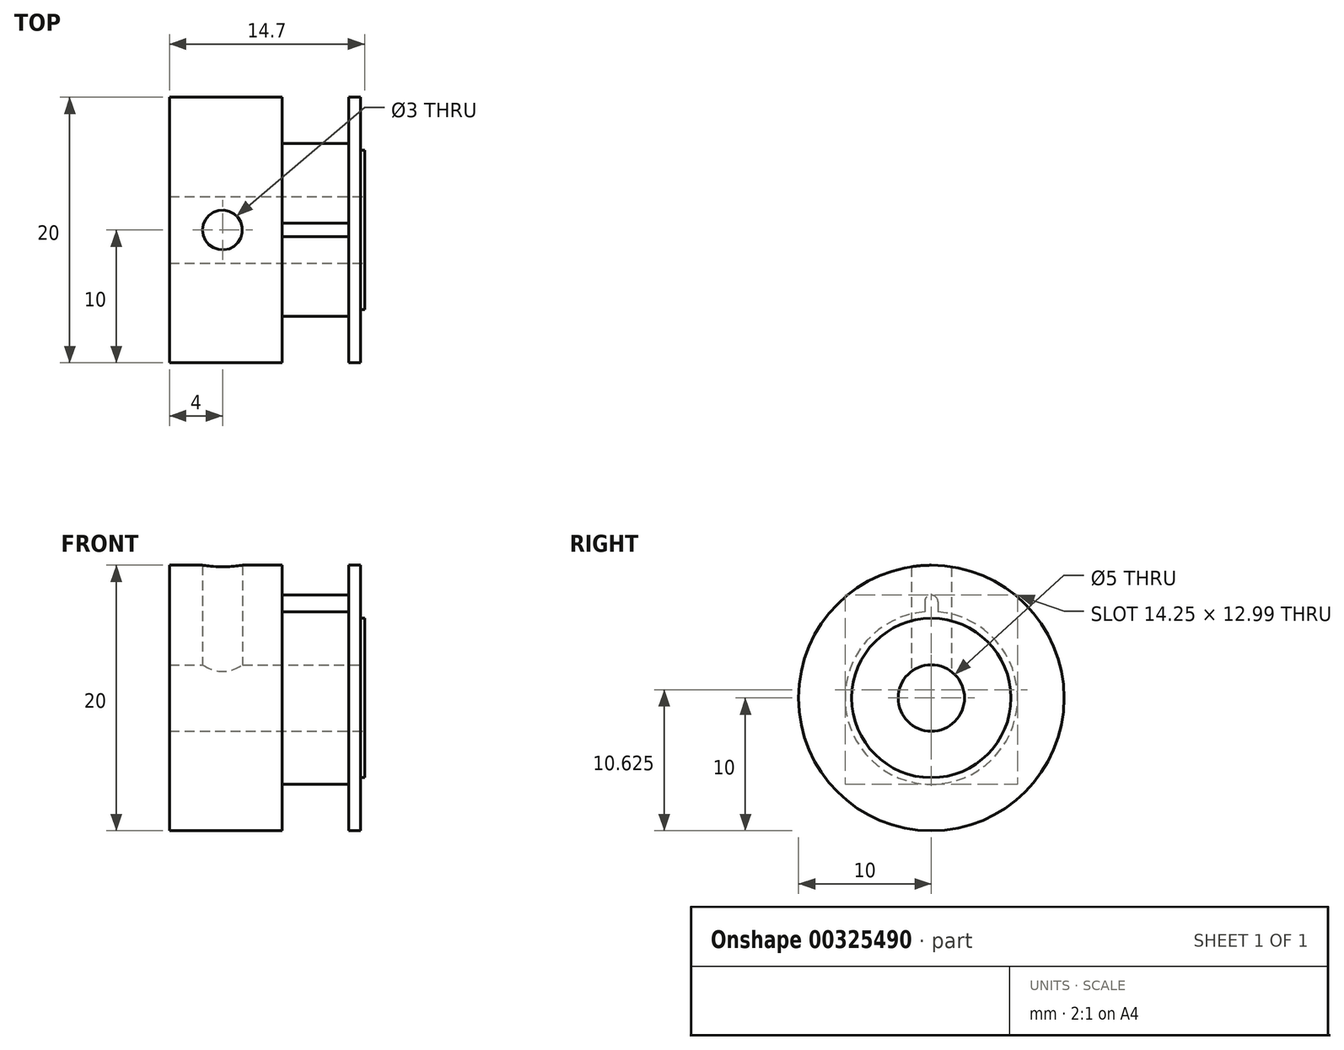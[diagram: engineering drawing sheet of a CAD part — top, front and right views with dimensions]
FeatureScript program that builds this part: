
annotation { "Feature Type Name" : "Feature", "Feature Type Description" : "" }
export const myFeature = defineFeature(function(context is Context, id is Id, definition is map)
    precondition{}
    {
        {
            var Q0;
            Q0=qCreatedBy(makeId("Right.planeOp"),FACE);
            var sketch = newSketch(context, id + "F0", { "sketchPlane" : qUnion([Q0])});
            skCircle(sketch, "E0", {"center": v(0, 0) * mm, "radius": 10 * mm});
            skSolve(sketch);
        }
        {
            var Q0;
            Q0 = qSketchRegion(id + "F0", true);
            extrude(context, id + "F1", {"entities" : qUnion([Q0]), "depth" : 8.5 * mm});
        }
        {
            var Q0;
            Q0=makeQuery(id+"F1.opExtrude","CAP_FACE",FACE,{"disambiguationData":[OSD([sQuery(id+"F0.wireOp",EDGE,"E0")])],"isStart":false});
            var sketch = newSketch(context, id + "F2", { "sketchPlane" : qUnion([Q0])});
            skLineSegment(sketch, "E1", {"start": v(0, 0) * mm, "end": v(0, 7.25) * mm, "construction": true});
            skArc(sketch, "E2", {"start": v(0.5, 7.25) * mm, "mid": v(0, 7.75) * mm, "end": v(-0.5, 7.25) * mm});
            skLineSegment(sketch, "E3", {"start": v(10, 0) * mm, "end": v(-10, 0) * mm, "construction": true});
            skArc(sketch, "E4", {"start": v(-0.5, 6.48) * mm, "mid": v(0, -6.5) * mm, "end": v(0.5, 6.48) * mm});
            skLineSegment(sketch, "E5", {"start": v(0.5, 7.25) * mm, "end": v(0.5, 6.48) * mm});
            skLineSegment(sketch, "E6", {"start": v(-0.5, 7.25) * mm, "end": v(-0.5, 6.48) * mm});
            skSolve(sketch);
        }
        {
            var Q0;
            Q0 = qSketchRegion(id + "F2", true);
            extrude(context, id + "F3", {"entities" : qUnion([Q0]), "operationType" : NewBodyOperationType.ADD, "depth" : 5 * mm});
        }
        {
            var Q0;
            Q0=qCreatedBy(makeId("Top.planeOp"),FACE);
            var sketch = newSketch(context, id + "F4", { "sketchPlane" : qUnion([Q0])});
            skLineSegment(sketch, "E7", {"start": v(0, 0) * mm, "end": v(13.5, 0) * mm, "construction": true});
            skSolve(sketch);
        }
        {
            var Q0;
            {var subQ0=sQuery(id+"F2.wireOp",EDGE,"E6");var subQ1=sQuery(id+"F2.wireOp",EDGE,"E5");var subQ2=sQuery(id+"F2.wireOp",EDGE,"E4");var subQ3=sQuery(id+"F2.wireOp",EDGE,"E2");Q0=makeQuery(id+"FyRSQMwNCxiUzVp_1.19.F3.boolean.opBoolean","MERGE",FACE,{"derivedFrom":[makeQuery(id+"FyRSQMwNCxiUzVp_1.18.F3.boolean.opBoolean","MERGE",FACE,{"derivedFrom":[makeQuery(id+"FyRSQMwNCxiUzVp_1.17.F3.boolean.opBoolean","MERGE",FACE,{"derivedFrom":[makeQuery(id+"FyRSQMwNCxiUzVp_1.16.F3.boolean.opBoolean","MERGE",FACE,{"derivedFrom":[makeQuery(id+"FyRSQMwNCxiUzVp_1.15.F3.boolean.opBoolean","MERGE",FACE,{"derivedFrom":[makeQuery(id+"FyRSQMwNCxiUzVp_1.14.F3.boolean.opBoolean","MERGE",FACE,{"derivedFrom":[makeQuery(id+"FyRSQMwNCxiUzVp_1.13.F3.boolean.opBoolean","MERGE",FACE,{"derivedFrom":[makeQuery(id+"FyRSQMwNCxiUzVp_1.12.F3.boolean.opBoolean","MERGE",FACE,{"derivedFrom":[makeQuery(id+"FyRSQMwNCxiUzVp_1.11.F3.boolean.opBoolean","MERGE",FACE,{"derivedFrom":[makeQuery(id+"FyRSQMwNCxiUzVp_1.10.F3.boolean.opBoolean","MERGE",FACE,{"derivedFrom":[makeQuery(id+"FyRSQMwNCxiUzVp_1.9.F3.boolean.opBoolean","MERGE",FACE,{"derivedFrom":[makeQuery(id+"FyRSQMwNCxiUzVp_1.8.F3.boolean.opBoolean","MERGE",FACE,{"derivedFrom":[makeQuery(id+"FyRSQMwNCxiUzVp_1.7.F3.boolean.opBoolean","MERGE",FACE,{"derivedFrom":[makeQuery(id+"FyRSQMwNCxiUzVp_1.6.F3.boolean.opBoolean","MERGE",FACE,{"derivedFrom":[makeQuery(id+"FyRSQMwNCxiUzVp_1.5.F3.boolean.opBoolean","MERGE",FACE,{"derivedFrom":[makeQuery(id+"FyRSQMwNCxiUzVp_1.4.F3.boolean.opBoolean","MERGE",FACE,{"derivedFrom":[makeQuery(id+"FyRSQMwNCxiUzVp_1.3.F3.boolean.opBoolean","MERGE",FACE,{"derivedFrom":[makeQuery(id+"FyRSQMwNCxiUzVp_1.2.F3.boolean.opBoolean","MERGE",FACE,{"derivedFrom":[makeQuery(id+"FyRSQMwNCxiUzVp_1.1.F3.boolean.opBoolean","MERGE",FACE,{"derivedFrom":[makeQuery(id+"F3.opExtrude","CAP_FACE",FACE,{"disambiguationData":[OSD([subQ3,subQ2,subQ1,subQ0])],"isStart":false}),makeQuery(id+"FyRSQMwNCxiUzVp_1.1.F3.opExtrude","CAP_FACE",FACE,{"disambiguationData":[OSD([subQ3,subQ2,subQ1,subQ0])],"isStart":false})]}),makeQuery(id+"FyRSQMwNCxiUzVp_1.2.F3.opExtrude","CAP_FACE",FACE,{"disambiguationData":[OSD([subQ3,subQ2,subQ1,subQ0])],"isStart":false})]}),makeQuery(id+"FyRSQMwNCxiUzVp_1.3.F3.opExtrude","CAP_FACE",FACE,{"disambiguationData":[OSD([subQ3,subQ2,subQ1,subQ0])],"isStart":false})]}),makeQuery(id+"FyRSQMwNCxiUzVp_1.4.F3.opExtrude","CAP_FACE",FACE,{"disambiguationData":[OSD([subQ3,subQ2,subQ1,subQ0])],"isStart":false})]}),makeQuery(id+"FyRSQMwNCxiUzVp_1.5.F3.opExtrude","CAP_FACE",FACE,{"disambiguationData":[OSD([subQ3,subQ2,subQ1,subQ0])],"isStart":false})]}),makeQuery(id+"FyRSQMwNCxiUzVp_1.6.F3.opExtrude","CAP_FACE",FACE,{"disambiguationData":[OSD([subQ3,subQ2,subQ1,subQ0])],"isStart":false})]}),makeQuery(id+"FyRSQMwNCxiUzVp_1.7.F3.opExtrude","CAP_FACE",FACE,{"disambiguationData":[OSD([subQ3,subQ2,subQ1,subQ0])],"isStart":false})]}),makeQuery(id+"FyRSQMwNCxiUzVp_1.8.F3.opExtrude","CAP_FACE",FACE,{"disambiguationData":[OSD([subQ3,subQ2,subQ1,subQ0])],"isStart":false})]}),makeQuery(id+"FyRSQMwNCxiUzVp_1.9.F3.opExtrude","CAP_FACE",FACE,{"disambiguationData":[OSD([subQ3,subQ2,subQ1,subQ0])],"isStart":false})]}),makeQuery(id+"FyRSQMwNCxiUzVp_1.10.F3.opExtrude","CAP_FACE",FACE,{"disambiguationData":[OSD([subQ3,subQ2,subQ1,subQ0])],"isStart":false})]}),makeQuery(id+"FyRSQMwNCxiUzVp_1.11.F3.opExtrude","CAP_FACE",FACE,{"disambiguationData":[OSD([subQ3,subQ2,subQ1,subQ0])],"isStart":false})]}),makeQuery(id+"FyRSQMwNCxiUzVp_1.12.F3.opExtrude","CAP_FACE",FACE,{"disambiguationData":[OSD([subQ3,subQ2,subQ1,subQ0])],"isStart":false})]}),makeQuery(id+"FyRSQMwNCxiUzVp_1.13.F3.opExtrude","CAP_FACE",FACE,{"disambiguationData":[OSD([subQ3,subQ2,subQ1,subQ0])],"isStart":false})]}),makeQuery(id+"FyRSQMwNCxiUzVp_1.14.F3.opExtrude","CAP_FACE",FACE,{"disambiguationData":[OSD([subQ3,subQ2,subQ1,subQ0])],"isStart":false})]}),makeQuery(id+"FyRSQMwNCxiUzVp_1.15.F3.opExtrude","CAP_FACE",FACE,{"disambiguationData":[OSD([subQ3,subQ2,subQ1,subQ0])],"isStart":false})]}),makeQuery(id+"FyRSQMwNCxiUzVp_1.16.F3.opExtrude","CAP_FACE",FACE,{"disambiguationData":[OSD([subQ3,subQ2,subQ1,subQ0])],"isStart":false})]}),makeQuery(id+"FyRSQMwNCxiUzVp_1.17.F3.opExtrude","CAP_FACE",FACE,{"disambiguationData":[OSD([subQ3,subQ2,subQ1,subQ0])],"isStart":false})]}),makeQuery(id+"FyRSQMwNCxiUzVp_1.18.F3.opExtrude","CAP_FACE",FACE,{"disambiguationData":[OSD([subQ3,subQ2,subQ1,subQ0])],"isStart":false})]}),makeQuery(id+"FyRSQMwNCxiUzVp_1.19.F3.opExtrude","CAP_FACE",FACE,{"disambiguationData":[OSD([subQ3,subQ2,subQ1,subQ0])],"isStart":false})]});}
            var sketch = newSketch(context, id + "F5", { "sketchPlane" : qUnion([Q0])});
            skCircle(sketch, "E8", {"center": v(0, 0) * mm, "radius": 10 * mm});
            skSolve(sketch);
        }
        {
            var Q0;
            Q0 = qSketchRegion(id + "F5", true);
            extrude(context, id + "F6", {"entities" : qUnion([Q0]), "operationType" : NewBodyOperationType.ADD, "depth" : 0.9 * mm});
        }
        {
            var Q0;
            Q0=makeQuery(id+"F6.opExtrude","CAP_FACE",FACE,{"disambiguationData":[OSD([sQuery(id+"F5.wireOp",EDGE,"E8")])],"isStart":false});
            var sketch = newSketch(context, id + "F7", { "sketchPlane" : qUnion([Q0])});
            skCircle(sketch, "E9", {"center": v(0, 0) * mm, "radius": 6 * mm});
            skSolve(sketch);
        }
        {
            var Q0;
            Q0 = qSketchRegion(id + "F7", true);
            extrude(context, id + "F8", {"entities" : qUnion([Q0]), "operationType" : NewBodyOperationType.ADD, "depth" : 0.3 * mm});
        }
        {
            var Q0;
            Q0=makeQuery(id+"F8.opExtrude","CAP_FACE",FACE,{"disambiguationData":[OSD([sQuery(id+"F7.wireOp",EDGE,"E9")])],"isStart":false});
            var sketch = newSketch(context, id + "F9", { "sketchPlane" : qUnion([Q0])});
            skCircle(sketch, "E10", {"center": v(0, 0) * mm, "radius": 2.5 * mm});
            skSolve(sketch);
        }
        {
            var Q0;
            Q0 = qSketchRegion(id + "F9", true);
            extrude(context, id + "F10", {"entities" : qUnion([Q0]), "operationType" : NewBodyOperationType.REMOVE, "endBound" : BoundingType.UP_TO_NEXT, "oppositeDirection" : true, "depth" : 25 * mm});
        }
        {
            var Q0;
            Q0=qCreatedBy(makeId("Top.planeOp"),FACE);
            var sketch = newSketch(context, id + "F11", { "sketchPlane" : qUnion([Q0])});
            skCircle(sketch, "E11", {"center": v(4, 0) * mm, "radius": 1.5 * mm});
            skSolve(sketch);
        }
        {
            var Q0;
            Q0 = qSketchRegion(id + "F11", true);
            var Q1;
            Q1=makeQuery(id+"F1.opExtrude","SWEPT_FACE",FACE,{"disambiguationData":[OSD([sQuery(id+"F0.wireOp",EDGE,"E0")])]});
            extrude(context, id + "F12", {"entities" : qUnion([Q0]), "operationType" : NewBodyOperationType.REMOVE, "endBound" : BoundingType.UP_TO_SURFACE, "endBoundEntityFace" : qUnion([Q1]), "depth" : 25 * mm});
        }
    });
